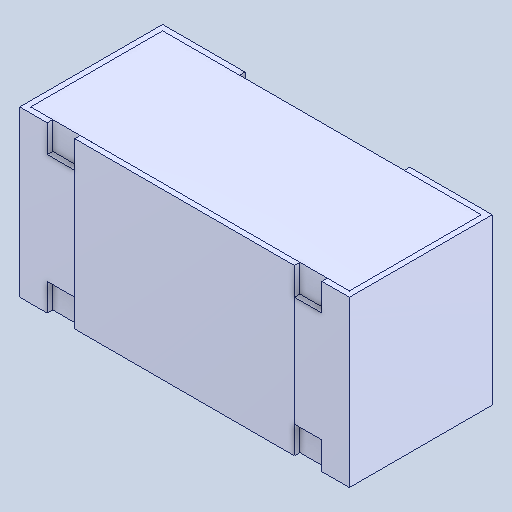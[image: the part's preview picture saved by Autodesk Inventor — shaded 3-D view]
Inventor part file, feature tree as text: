
AUTODESK INVENTOR PART (.ipt)
format: ipt  version: 2025 (Build 290162000, 162)  size: 113,152 bytes
history: native  units: mm
features: boolean_combine x2, other x1, mirror x1
ambient origin geometry x8: Origin, YZ Plane, XZ Plane, XY Plane, X Axis, Y Axis, Z Axis, Center Point
bodies: Solid1 (feature_tree), Solid2 (feature_tree), Solid3 (feature_tree), Solid4 (feature_tree)
feature tree (4):
  other  "Cut-Extrude1"
  boolean_combine  "Combine2"
  mirror  "Mirror1[3]"
  boolean_combine  "Combine1"
